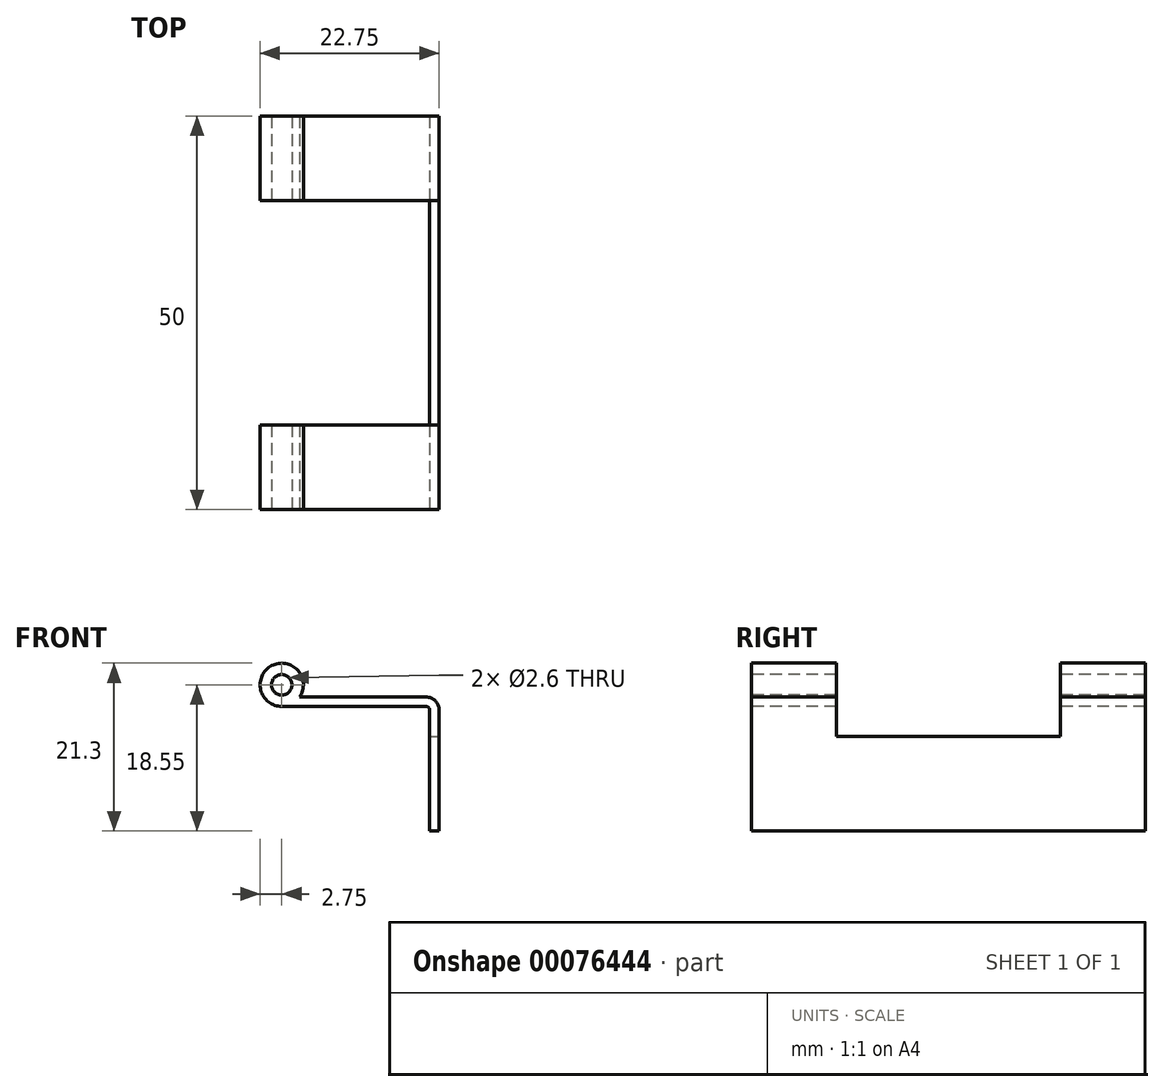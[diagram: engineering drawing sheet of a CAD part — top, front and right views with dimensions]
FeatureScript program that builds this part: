
annotation { "Feature Type Name" : "Feature", "Feature Type Description" : "" }
export const myFeature = defineFeature(function(context is Context, id is Id, definition is map)
    precondition{}
    {
        {
            var Q0;
            Q0=qCreatedBy(makeId("Front.planeOp"),FACE);
            var sketch = newSketch(context, id + "F0", { "sketchPlane" : qUnion([Q0])});
            skCircle(sketch, "E0", {"center": v(0, 0) * mm, "radius": 2.75 * mm});
            skLineSegment(sketch, "E1", {"start": v(0, -2.75) * mm, "end": v(18.3, -2.75) * mm});
            skLineSegment(sketch, "E2", {"start": v(18.8, -3.25) * mm, "end": v(18.8, -18.55) * mm});
            skPoint(sketch, "E3.visualSharp", {"position": v(18.8, -2.75) * mm});
            skArc(sketch, "E3.filletArc", {"start": v(18.8, -3.25) * mm, "mid": v(18.65, -2.9) * mm, "end": v(18.3, -2.75) * mm});
            skLineSegment(sketch, "E4.0", {"start": v(20, -3.25) * mm, "end": v(20, -18.55) * mm});
            skArc(sketch, "E4.1", {"start": v(20, -3.25) * mm, "mid": v(19.5, -2.05) * mm, "end": v(18.3, -1.55) * mm});
            skLineSegment(sketch, "E4.2", {"start": v(0, -1.55) * mm, "end": v(18.3, -1.55) * mm});
            skLineSegment(sketch, "E5", {"start": v(18.8, -18.55) * mm, "end": v(20, -18.55) * mm});
            skSolve(sketch);
        }
        {
            var Q0;
            {var subQ0=sQuery(id+"F0.wireOp",EDGE,"E1");Q0=makeQuery(id+"F0.imprint","IMPRINT",FACE,{"disambiguationData":[TD([[makeQuery(id+"F0.imprint","IMPRINT",EDGE,{"derivedFrom":subQ0}),1.0]])]});}
            var Q1;
            {var subQ0=sQuery(id+"F0.wireOp",EDGE,"E0");var subQ1=makeQuery(id+"F0.imprint","INTERSECT",VERTEX,{"derivedFrom":[subQ0,sQuery(id+"F0.wireOp",EDGE,"E1")]});Q1=makeQuery(id+"F0.imprint","IMPRINT",FACE,{"disambiguationData":[TD([[makeQuery(id+"F0.imprint","IMPRINT",EDGE,{"disambiguationData":[TD([[subQ1,-1.0]])],"derivedFrom":subQ0}),1.0]])]});}
            extrude(context, id + "F1", {"entities" : qUnion([Q0, Q1]), "oppositeDirection" : true, "depth" : 50 * mm});
        }
        {
            var Q0;
            Q0=sQuery(id+"F0.wireOp",VERTEX,"E0.center");
            var Q1;
            Q1=makeQuery(id+"F1.opExtrude","SWEPT_BODY",BODY,{"disambiguationData":[OSD([sQuery(id+"F0.wireOp",EDGE,"E0"),sQuery(id+"F0.wireOp",EDGE,"E1"),sQuery(id+"F0.wireOp",EDGE,"E2"),sQuery(id+"F0.wireOp",EDGE,"E3.filletArc"),sQuery(id+"F0.wireOp",EDGE,"E4.0"),sQuery(id+"F0.wireOp",EDGE,"E4.1"),sQuery(id+"F0.wireOp",EDGE,"E4.2"),sQuery(id+"F0.wireOp",EDGE,"E5")])]});
            hole(context, id + "F2", {"style" : HoleStyle.SIMPLE, "endStyle" : HoleEndStyle.THROUGH, "standardTappedOrClearance" : lookupTablePath({ "standard" : "ISO", "size" : "2.6", "type" : "Drilled" }), "standardBlindInLast" : lookupTablePath({ "standard" : "ISO", "size" : "2.6", "type" : "Drilled" }), "holeDiameter" : 2.6 * mm, "startFromSketch" : true, "locations" : qUnion([Q0]), "scope" : qUnion([Q1]), "isTappedThrough" : true});
        }
        {
            var Q0;
            Q0=makeQuery(id+"F1.opExtrude","SWEPT_FACE",FACE,{"disambiguationData":[OSD([sQuery(id+"F0.wireOp",EDGE,"E4.0")])]});
            var sketch = newSketch(context, id + "F3", { "sketchPlane" : qUnion([Q0])});
            skLineSegment(sketch, "E6.bottom", {"start": v(10.75, 3.45) * mm, "end": v(39.25, 3.45) * mm});
            skLineSegment(sketch, "E6.top", {"start": v(10.75, -6.55) * mm, "end": v(39.25, -6.55) * mm});
            skLineSegment(sketch, "E6.left", {"start": v(10.75, 3.45) * mm, "end": v(10.75, -6.55) * mm});
            skLineSegment(sketch, "E6.right", {"start": v(39.25, 3.45) * mm, "end": v(39.25, -6.55) * mm});
            skLineSegment(sketch, "E7", {"start": v(25, -18.55) * mm, "end": v(25, 3.37) * mm, "construction": true});
            skPoint(sketch, "E7.startSnap0", {"position": v(25, -6.55) * mm});
            skSolve(sketch);
        }
        {
            var Q0;
            {var subQ0=sQuery(id+"F3.wireOp",EDGE,"E6.bottom");Q0=makeQuery(id+"F3.imprint","IMPRINT",FACE,{"disambiguationData":[TD([[makeQuery(id+"F3.imprint","IMPRINT",EDGE,{"derivedFrom":subQ0}),-1.0]])]});}
            var Q1;
            {var subQ0=sQuery(id+"F3.wireOp",EDGE,"E6.top");Q1=makeQuery(id+"F3.imprint","IMPRINT",FACE,{"disambiguationData":[TD([[makeQuery(id+"F3.imprint","IMPRINT",EDGE,{"derivedFrom":subQ0}),1.0]])]});}
            extrude(context, id + "F4", {"entities" : qUnion([Q0, Q1]), "operationType" : NewBodyOperationType.REMOVE, "oppositeDirection" : true, "depth" : 25 * mm});
        }
    });
